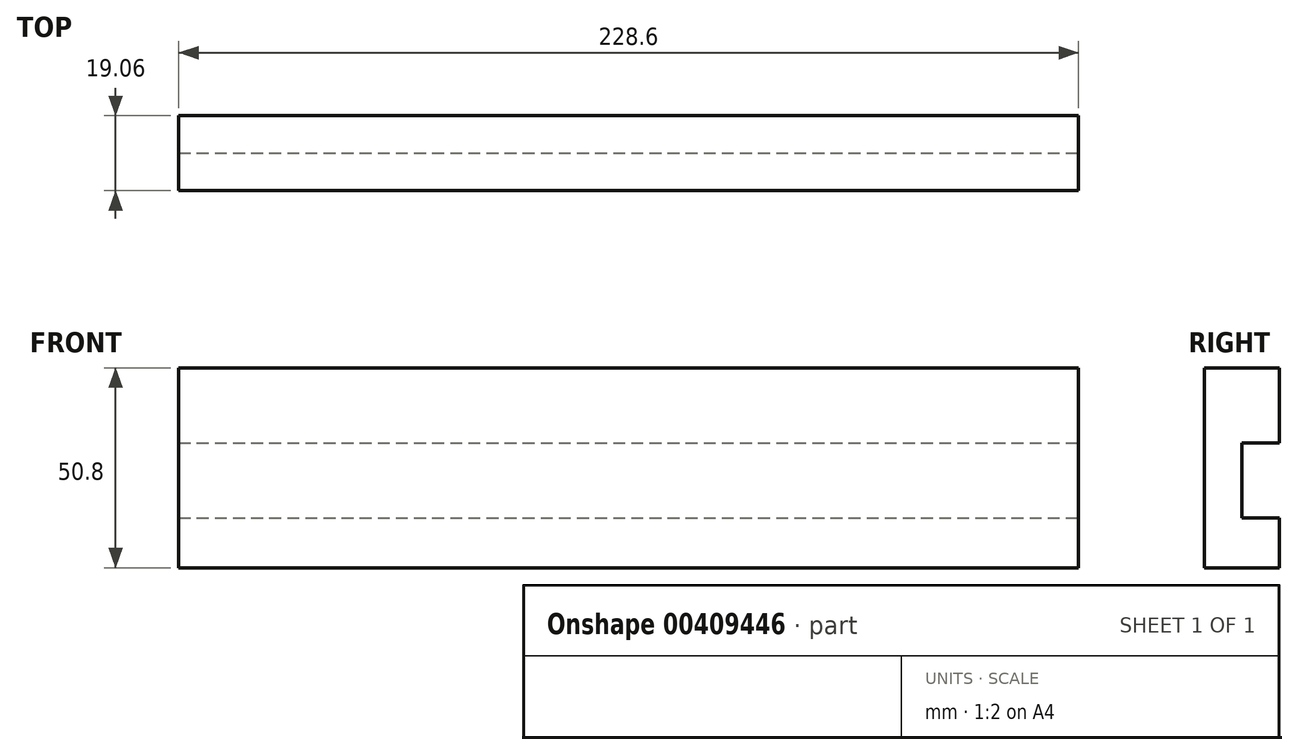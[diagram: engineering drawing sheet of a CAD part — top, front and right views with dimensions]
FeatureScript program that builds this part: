
annotation { "Feature Type Name" : "Feature", "Feature Type Description" : "" }
export const myFeature = defineFeature(function(context is Context, id is Id, definition is map)
    precondition{}
    {
        {
            var Q0;
            Q0=qCreatedBy(makeId("Front.planeOp"),FACE);
            var sketch = newSketch(context, id + "F0", { "sketchPlane" : qUnion([Q0])});
            skLineSegment(sketch, "E0.bottom", {"start": v(124.47, -4.31) * mm, "end": v(-104.13, -4.31) * mm});
            skLineSegment(sketch, "E0.top", {"start": v(124.47, 46.49) * mm, "end": v(-104.13, 46.49) * mm});
            skLineSegment(sketch, "E0.left", {"start": v(124.47, -4.31) * mm, "end": v(124.47, 46.49) * mm});
            skLineSegment(sketch, "E0.right", {"start": v(-104.13, -4.31) * mm, "end": v(-104.13, 46.49) * mm});
            skLineSegment(sketch, "E1.bottom", {"start": v(-104.13, 8.39) * mm, "end": v(124.47, 8.39) * mm});
            skLineSegment(sketch, "E1.top", {"start": v(-104.13, 27.44) * mm, "end": v(124.47, 27.44) * mm});
            skLineSegment(sketch, "E1.left", {"start": v(-104.13, 8.39) * mm, "end": v(-104.13, 27.44) * mm});
            skLineSegment(sketch, "E1.right", {"start": v(124.47, 8.39) * mm, "end": v(124.47, 27.44) * mm});
            skSolve(sketch);
        }
        {
            var Q0;
            {var subQ0=sQuery(id+"F0.wireOp",EDGE,"E0.top");Q0=makeQuery(id+"F0.imprint","IMPRINT",FACE,{"disambiguationData":[TD([[makeQuery(id+"F0.imprint","IMPRINT",EDGE,{"derivedFrom":subQ0}),1.0]])]});}
            var Q1;
            Q1=makeQuery(id+"F0.imprint","IMPRINT",FACE,{"disambiguationData":[TD([[makeQuery(id+"F0.imprint","IMPRINT",EDGE,{"derivedFrom":sQuery(id+"F0.wireOp",EDGE,"E1.bottom")}),1.0]])]});
            var Q2;
            {var subQ0=sQuery(id+"F0.wireOp",EDGE,"E0.bottom");Q2=makeQuery(id+"F0.imprint","IMPRINT",FACE,{"disambiguationData":[TD([[makeQuery(id+"F0.imprint","IMPRINT",EDGE,{"derivedFrom":subQ0}),-1.0]])]});}
            extrude(context, id + "F1", {"entities" : qUnion([Q0, Q1, Q2]), "depth" : 9.52 * mm});
        }
        {
            var Q0;
            {var subQ0=sQuery(id+"F0.wireOp",EDGE,"E0.bottom");Q0=makeQuery(id+"F0.imprint","IMPRINT",FACE,{"disambiguationData":[TD([[makeQuery(id+"F0.imprint","IMPRINT",EDGE,{"derivedFrom":subQ0}),-1.0]])]});}
            var Q1;
            {var subQ0=sQuery(id+"F0.wireOp",EDGE,"E0.top");Q1=makeQuery(id+"F0.imprint","IMPRINT",FACE,{"disambiguationData":[TD([[makeQuery(id+"F0.imprint","IMPRINT",EDGE,{"derivedFrom":subQ0}),1.0]])]});}
            extrude(context, id + "F2", {"entities" : qUnion([Q0, Q1]), "operationType" : NewBodyOperationType.ADD, "oppositeDirection" : true, "depth" : 9.52 * mm});
        }
    });
